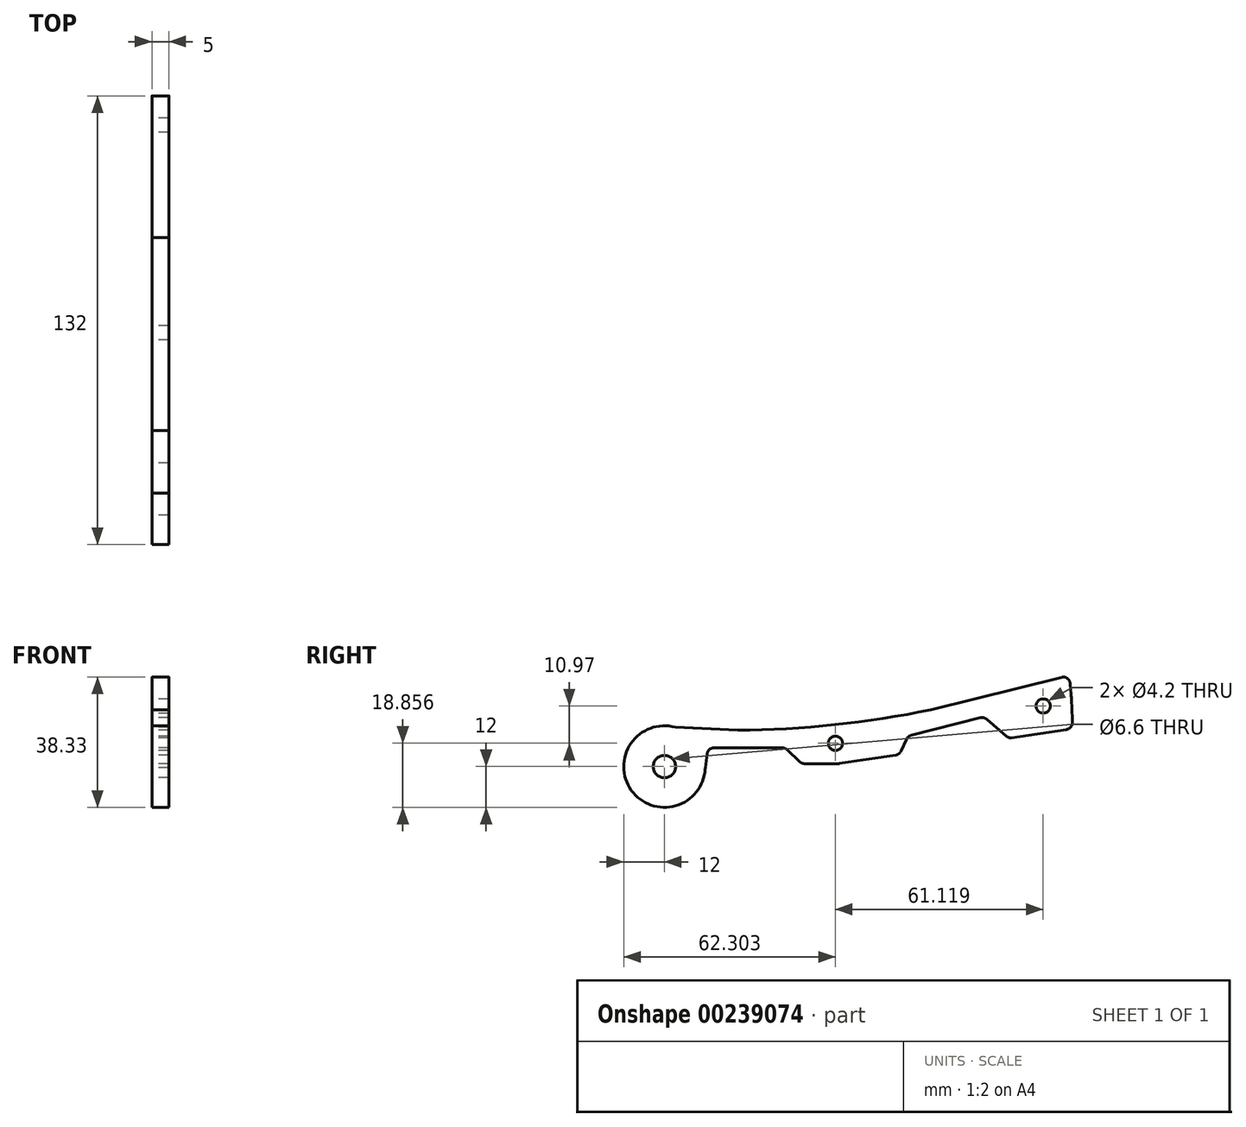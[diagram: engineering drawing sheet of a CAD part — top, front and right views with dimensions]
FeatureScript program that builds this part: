
annotation { "Feature Type Name" : "Feature", "Feature Type Description" : "" }
export const myFeature = defineFeature(function(context is Context, id is Id, definition is map)
    precondition{}
    {
        {
            var Q0;
            Q0=qCreatedBy(makeId("Right.planeOp"),FACE);
            var sketch = newSketch(context, id + "F0", { "sketchPlane" : qUnion([Q0])});
            skLineSegment(sketch, "E0", {"start": v(0, 0) * mm, "end": v(3.3, 0) * mm});
            skArc(sketch, "E1", {"start": v(21.96, 10.72) * mm, "mid": v(21.96, 10.73) * mm, "end": v(21.96, 10.73) * mm});
            skArc(sketch, "E2", {"start": v(120, 12.9) * mm, "mid": v(119.81, 18.73) * mm, "end": v(119.34, 24.54) * mm});
            skArc(sketch, "E3", {"start": v(21.46, 10.73) * mm, "mid": v(22.07, 10.72) * mm, "end": v(22.67, 10.8) * mm});
            skLineSegment(sketch, "E4", {"start": v(21.83, 10.72) * mm, "end": v(-2.06, 11.82) * mm});
            skLineSegment(sketch, "E5", {"start": v(78.34, 16.72) * mm, "end": v(116.87, 26.27) * mm});
            skCircle(sketch, "E6", {"center": v(0, 0) * mm, "radius": 3.3 * mm});
            skPoint(sketch, "E7.orphan", {"position": v(21.83, 9.28) * mm});
            skPoint(sketch, "E8.third.point", {"position": v(50.09, 12.3) * mm});
            skPoint(sketch, "E8.third.point.positionSnap0", {"position": v(50.09, 13.72) * mm});
            skArc(sketch, "E9", {"start": v(21.58, 10.73) * mm, "mid": v(50.11, 12.3) * mm, "end": v(78.34, 16.72) * mm});
            skCircle(sketch, "E10", {"center": v(111.42, 17.83) * mm, "radius": 2.1 * mm});
            skCircle(sketch, "E11", {"center": v(50.3, 6.86) * mm, "radius": 2.1 * mm});
            skArc(sketch, "E12", {"start": v(3.14, 11.58) * mm, "mid": v(-9.74, -7) * mm, "end": v(11.98, -0.7) * mm});
            skLineSegment(sketch, "E13", {"start": v(118.3, 10.9) * mm, "end": v(102.16, 8.49) * mm});
            skLineSegment(sketch, "E14", {"start": v(51.16, 0.86) * mm, "end": v(41.18, 0.86) * mm});
            skPoint(sketch, "E15.visualSharp", {"position": v(11.97, 0.86) * mm});
            skArc(sketch, "E15.filletArc", {"start": v(12.07, -0.27) * mm, "mid": v(12, -0.48) * mm, "end": v(11.98, -0.7) * mm});
            skLineSegment(sketch, "E16", {"start": v(14.57, 5.48) * mm, "end": v(34.75, 5.48) * mm});
            skLineSegment(sketch, "E17", {"start": v(72.52, 9.15) * mm, "end": v(93, 14.35) * mm});
            skLineSegment(sketch, "E18", {"start": v(12.58, 3.74) * mm, "end": v(11.97, -1.01) * mm});
            skLineSegment(sketch, "E19", {"start": v(36.13, 4.93) * mm, "end": v(39.8, 1.42) * mm});
            skLineSegment(sketch, "E20", {"start": v(69.56, 4.51) * mm, "end": v(71.2, 8.05) * mm});
            skLineSegment(sketch, "E21", {"start": v(94.8, 13.92) * mm, "end": v(100.56, 8.95) * mm});
            skLineSegment(sketch, "E22.trimOffspring", {"start": v(68.04, 3.37) * mm, "end": v(51.45, 0.89) * mm});
            skPoint(sketch, "E23.visualSharp", {"position": v(119.08, 26.82) * mm});
            skArc(sketch, "E23.filletArc", {"start": v(119.34, 24.54) * mm, "mid": v(118.5, 25.97) * mm, "end": v(116.87, 26.27) * mm});
            skPoint(sketch, "E24.visualSharp", {"position": v(12.8, 5.48) * mm});
            skArc(sketch, "E24.filletArc", {"start": v(14.57, 5.48) * mm, "mid": v(13.25, 4.99) * mm, "end": v(12.58, 3.74) * mm});
            skPoint(sketch, "E25.visualSharp", {"position": v(35.55, 5.48) * mm});
            skArc(sketch, "E25.filletArc", {"start": v(36.13, 4.93) * mm, "mid": v(35.5, 5.34) * mm, "end": v(34.75, 5.48) * mm});
            skPoint(sketch, "E26.visualSharp", {"position": v(40.38, 0.86) * mm});
            skArc(sketch, "E26.filletArc", {"start": v(39.8, 1.42) * mm, "mid": v(40.43, 1) * mm, "end": v(41.18, 0.86) * mm});
            skPoint(sketch, "E27.visualSharp", {"position": v(120, 11.16) * mm});
            skArc(sketch, "E27.filletArc", {"start": v(118.3, 10.9) * mm, "mid": v(119.52, 11.58) * mm, "end": v(120, 12.9) * mm});
            skPoint(sketch, "E28.visualSharp", {"position": v(101.25, 8.35) * mm});
            skArc(sketch, "E28.filletArc", {"start": v(100.56, 8.95) * mm, "mid": v(101.3, 8.54) * mm, "end": v(102.16, 8.49) * mm});
            skPoint(sketch, "E29.visualSharp", {"position": v(94.01, 14.6) * mm});
            skArc(sketch, "E29.filletArc", {"start": v(94.8, 13.92) * mm, "mid": v(93.95, 14.35) * mm, "end": v(93, 14.35) * mm});
            skPoint(sketch, "E30.visualSharp", {"position": v(71.6, 8.92) * mm});
            skArc(sketch, "E30.filletArc", {"start": v(72.52, 9.15) * mm, "mid": v(71.73, 8.75) * mm, "end": v(71.2, 8.05) * mm});
            skPoint(sketch, "E31.visualSharp", {"position": v(69.11, 3.53) * mm});
            skArc(sketch, "E31.filletArc", {"start": v(68.04, 3.37) * mm, "mid": v(68.95, 3.75) * mm, "end": v(69.56, 4.51) * mm});
            skPoint(sketch, "E32.visualSharp", {"position": v(51.3, 0.86) * mm});
            skArc(sketch, "E32.filletArc", {"start": v(51.16, 0.86) * mm, "mid": v(51.3, 0.87) * mm, "end": v(51.45, 0.89) * mm});
            skSolve(sketch);
        }
        {
            var Q0;
            {var subQ9=sQuery(id+"F0.wireOp",EDGE,"Z2RfFS8F-fJbA-lgiH-K7Vn-SxlDWFhEWRw2");Q0=makeQuery(id+"F0.imprint","IMPRINT",FACE,{"disambiguationData":[TD([[makeQuery(id+"F0.imprint","IMPRINT",EDGE,{"derivedFrom":subQ9}),-1.0]])]});}
            var Q1;
            Q1=qSketchRegion(id+"F0",true);
            extrude(context, id + "F1", {"entities" : qUnion([Q0, Q1]), "depth" : 5 * mm});
        }
    });
